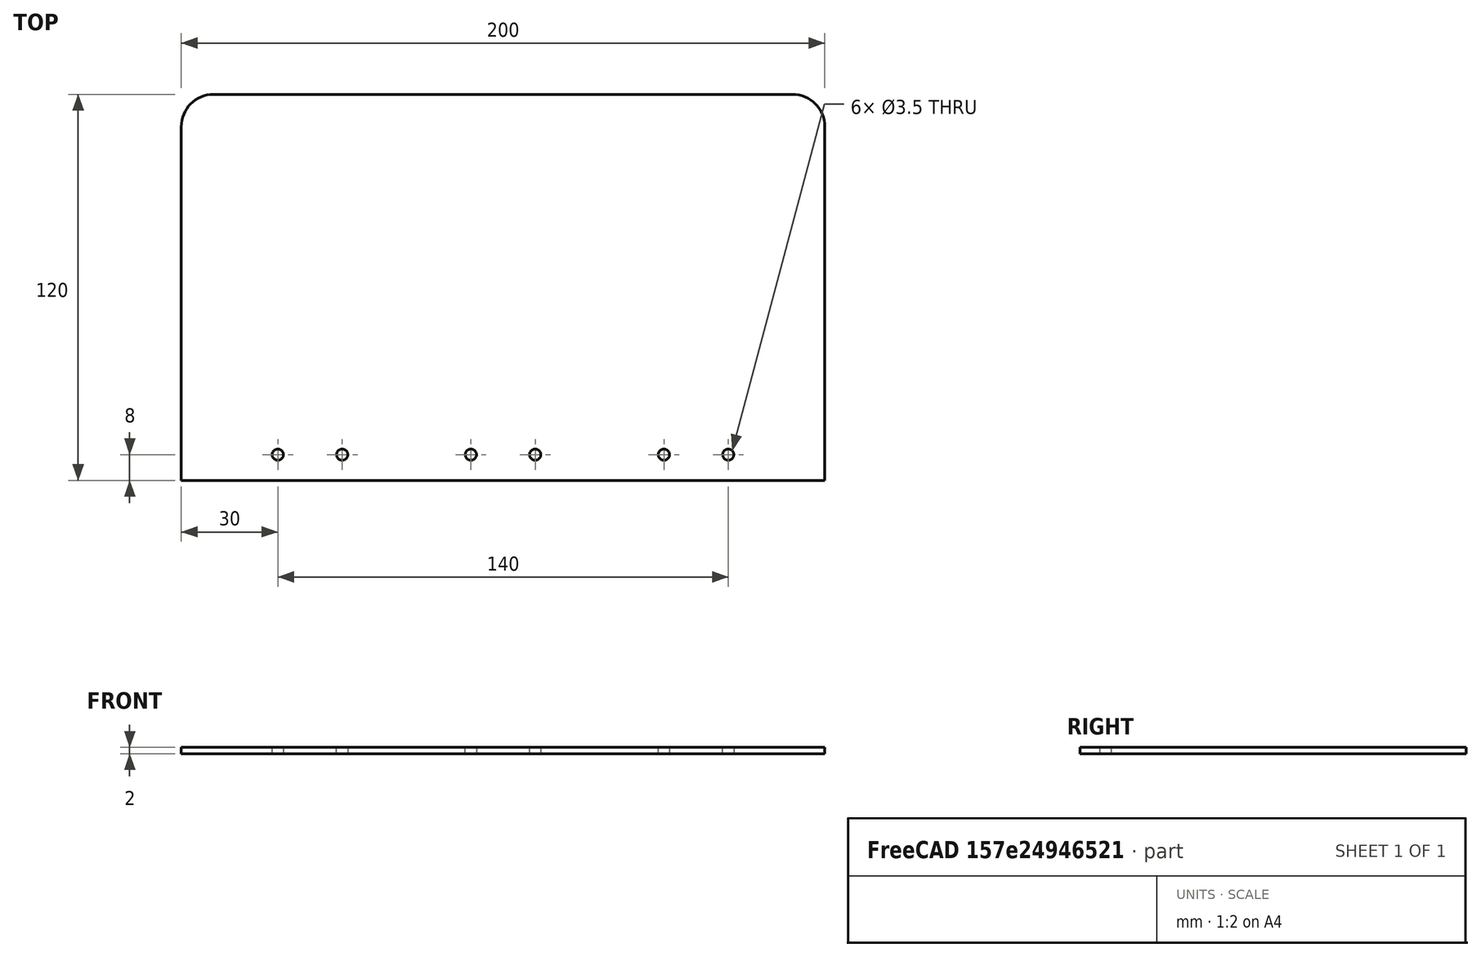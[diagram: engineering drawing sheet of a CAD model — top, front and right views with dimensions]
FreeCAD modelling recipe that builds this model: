
FCSTD DOCUMENT  (FreeCAD 0.20R29603 (Git))
Label: BackplaneFrontPanel
License: All rights reserved
LicenseURL: http://en.wikipedia.org/wiki/All_rights_reserved
objects: Sketcher::SketchObject×2, PartDesign::Pad×1, PartDesign::Pocket×1, PartDesign::Body×1, Mesh::Feature×1
note: 7 computed .brp shape members not serialized (recipe doc carries the construction recipe); baked Part::Feature solids carry a one-line shape summary decoded from their .brp

FEATURE [Sketcher::SketchObject] Sketch
  FullyConstrained = true
  MapMode = 5
  Support = -> [XY_Plane]
  sketch-geometry (8):
    g0: LineSegment StartX=0 StartY=0 StartZ=0 EndX=200 EndY=0 EndZ=0
    g1: LineSegment StartX=200 StartY=0 StartZ=0 EndX=200 EndY=110 EndZ=0
    g2: LineSegment StartX=190 StartY=120 StartZ=0 EndX=10 EndY=120 EndZ=0
    g3: LineSegment StartX=0 StartY=110 StartZ=0 EndX=0 EndY=0 EndZ=0
    g4: ArcOfCircle CenterX=10 CenterY=110 CenterZ=0 NormalX=0 NormalY=0 NormalZ=1 AngleXU=0 Radius=10 StartAngle=1.5708 EndAngle=3.14159
    g5: GeomPoint X=0 Y=120 Z=0
    g6: ArcOfCircle CenterX=190 CenterY=110 CenterZ=0 NormalX=0 NormalY=0 NormalZ=1 AngleXU=0 Radius=10 StartAngle=0 EndAngle=1.5708
    g7: GeomPoint X=200 Y=120 Z=0
  constraints (19):
    c: Coincident(g0,g1)
    c: Coincident(g3,g0)
    c: Horizontal(g0)
    c: Horizontal(g2)
    c: Vertical(g1)
    c: Vertical(g3)
    c: Coincident(g0,g-1)
    c: PointOnObject(g5,g3)
    c: PointOnObject(g5,g2)
    c: Tangent(g3,g4) = -1.5708
    c: Tangent(g2,g4) = -1.5708
    c: PointOnObject(g7,g2)
    c: PointOnObject(g7,g1)
    c: Tangent(g2,g6) = -1.5708
    c: Tangent(g1,g6) = -1.5708
    c: Radius(g6) = 10
    c: Radius(g4) = 10
    c: Distance(g0,g0) = 200
    c: Distance(g2,g0) = 120
FEATURE [PartDesign::Pad] Pad
  Direction = (0,0,1)
  Length = 2
  Length2 = 10
  Profile = -> Sketch
  ReferenceAxis = -> Sketch [N_Axis]
  Type = 0
FEATURE [Sketcher::SketchObject] Sketch001
  ExternalGeometry = -> [Pad]
  FullyConstrained = true
  MapMode = 5
  Placement = pos=(0,0,2) rot=(0,0,1;0rad)
  Support = -> [Pad]
  sketch-geometry (6):
    g0: Circle CenterX=50 CenterY=8 CenterZ=0 NormalX=0 NormalY=0 NormalZ=1 AngleXU=0 Radius=1.75
    g1: Circle CenterX=30 CenterY=8 CenterZ=0 NormalX=0 NormalY=0 NormalZ=1 AngleXU=0 Radius=1.75
    g2: Circle CenterX=90 CenterY=8 CenterZ=0 NormalX=0 NormalY=0 NormalZ=1 AngleXU=0 Radius=1.75
    g3: Circle CenterX=110 CenterY=8 CenterZ=0 NormalX=0 NormalY=0 NormalZ=1 AngleXU=0 Radius=1.75
    g4: Circle CenterX=150 CenterY=8 CenterZ=0 NormalX=0 NormalY=0 NormalZ=1 AngleXU=0 Radius=1.75
    g5: Circle CenterX=170 CenterY=8 CenterZ=0 NormalX=0 NormalY=0 NormalZ=1 AngleXU=0 Radius=1.75
  constraints (18):
    c: Distance(g1,g-3) = 8
    c: Distance(g0,g-3) = 8
    c: Distance(g2,g-3) = 8
    c: Distance(g3,g-3) = 8
    c: Distance(g4,g-3) = 8
    c: Distance(g5,g-3) = 8
    c: Diameter(g1) = 3.5
    c: Diameter(g0) = 3.5
    c: Diameter(g2) = 3.5
    c: Diameter(g3) = 3.5
    c: Diameter(g4) = 3.5
    c: Diameter(g5) = 3.5
    c: Distance(g1,g-4) = 30
    c: Distance(g0,g-4) = 50
    c: Distance(g2,g-4) = 90
    c: Distance(g3,g-4) = 110
    c: Distance(g4,g-4) = 150
    c: Distance(g5,g-4) = 170
FEATURE [PartDesign::Pocket] Pocket
  BaseFeature = -> Pad
  Direction = (0,0,-1)
  Length = 5
  Length2 = 5
  Profile = -> Sketch001
  ReferenceAxis = -> Sketch001 [N_Axis]
  Type = 1
FEATURE [PartDesign::Body] Body
  Group = -> [Sketch,Pad,Sketch001,Pocket]
  Origin = -> Origin
  Tip = -> Pocket
FEATURE [Mesh::Feature] Mesh  label="Pocket (Meshed)"
